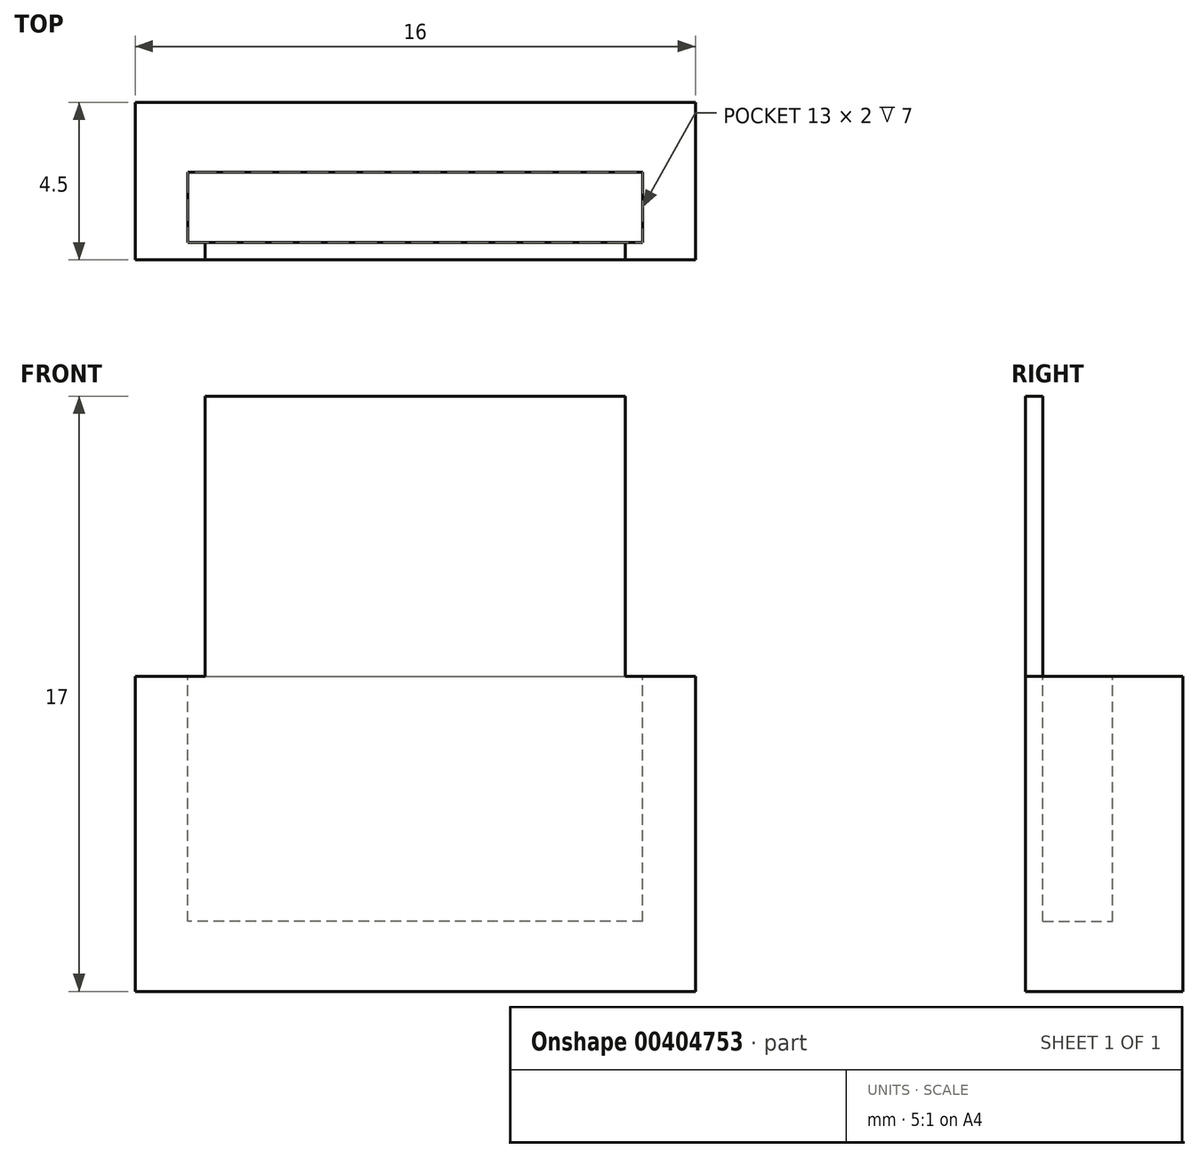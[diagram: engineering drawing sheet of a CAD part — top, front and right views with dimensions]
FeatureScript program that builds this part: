
annotation { "Feature Type Name" : "Feature", "Feature Type Description" : "" }
export const myFeature = defineFeature(function(context is Context, id is Id, definition is map)
    precondition{}
    {
        {
            var Q0;
            Q0=qCreatedBy(makeId("Top.planeOp"),FACE);
            var sketch = newSketch(context, id + "F0", { "sketchPlane" : qUnion([Q0])});
            skLineSegment(sketch, "E0.bottom", {"start": v(-8, 2.25) * mm, "end": v(8, 2.25) * mm});
            skLineSegment(sketch, "E0.top", {"start": v(-8, -2.25) * mm, "end": v(8, -2.25) * mm});
            skLineSegment(sketch, "E0.left", {"start": v(-8, 2.25) * mm, "end": v(-8, -2.25) * mm});
            skLineSegment(sketch, "E0.right", {"start": v(8, 2.25) * mm, "end": v(8, -2.25) * mm});
            skPoint(sketch, "E0.middle", {"position": v(0, 0) * mm});
            skSolve(sketch);
        }
        {
            var Q0;
            Q0 = qSketchRegion(id + "F0", true);
            extrude(context, id + "F1", {"entities" : qUnion([Q0]), "depth" : 9 * mm});
        }
        {
            var Q0;
            Q0=makeQuery(id+"F1.opExtrude","CAP_FACE",FACE,{"disambiguationData":[OSD([sQuery(id+"F0.wireOp",EDGE,"E0.bottom"),sQuery(id+"F0.wireOp",EDGE,"E0.top"),sQuery(id+"F0.wireOp",EDGE,"E0.left"),sQuery(id+"F0.wireOp",EDGE,"E0.right")])],"isStart":false});
            var sketch = newSketch(context, id + "F2", { "sketchPlane" : qUnion([Q0])});
            skLineSegment(sketch, "E1", {"start": v(-6.5, -1.75) * mm, "end": v(-6.5, 0.25) * mm});
            skLineSegment(sketch, "E2", {"start": v(-6.5, 0.25) * mm, "end": v(6.5, 0.25) * mm});
            skLineSegment(sketch, "E3", {"start": v(6.5, 0.25) * mm, "end": v(6.5, -1.75) * mm});
            skLineSegment(sketch, "E4", {"start": v(6.5, -1.75) * mm, "end": v(-6.5, -1.75) * mm});
            skSolve(sketch);
        }
        {
            var Q0;
            Q0 = qSketchRegion(id + "F2", true);
            extrude(context, id + "F3", {"entities" : qUnion([Q0]), "operationType" : NewBodyOperationType.REMOVE, "oppositeDirection" : true, "depth" : 7 * mm});
        }
        {
            var Q0;
            Q0=makeQuery(id+"F1.opExtrude","CAP_FACE",FACE,{"disambiguationData":[OSD([sQuery(id+"F0.wireOp",EDGE,"E0.bottom"),sQuery(id+"F0.wireOp",EDGE,"E0.top"),sQuery(id+"F0.wireOp",EDGE,"E0.left"),sQuery(id+"F0.wireOp",EDGE,"E0.right")])],"isStart":false});
            var sketch = newSketch(context, id + "F4", { "sketchPlane" : qUnion([Q0])});
            skLineSegment(sketch, "E5", {"start": v(-6, -1.75) * mm, "end": v(-6, -2.25) * mm});
            skLineSegment(sketch, "E6", {"start": v(-6, -2.25) * mm, "end": v(6, -2.25) * mm});
            skLineSegment(sketch, "E7", {"start": v(6, -2.25) * mm, "end": v(6, -1.75) * mm});
            skLineSegment(sketch, "E8", {"start": v(6, -1.75) * mm, "end": v(-6, -1.75) * mm});
            skSolve(sketch);
        }
        {
            var Q0;
            Q0=makeQuery(id+"F4.imprint","IMPRINT",FACE,{"disambiguationData":[TD([[makeQuery(id+"F4.imprint","IMPRINT",EDGE,{"derivedFrom":sQuery(id+"F4.wireOp",EDGE,"E5")}),1.0]])]});
            extrude(context, id + "F5", {"entities" : qUnion([Q0]), "operationType" : NewBodyOperationType.ADD, "depth" : 8 * mm});
        }
    });
